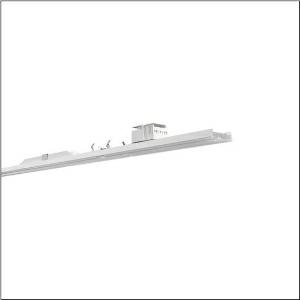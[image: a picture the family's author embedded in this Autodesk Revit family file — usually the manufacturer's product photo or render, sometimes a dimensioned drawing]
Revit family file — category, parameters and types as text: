
# Revit family: licross_r__11_recessed_mo_51tl18cn48xfd_9798
name_source: partatom
category: Lighting Fixtures
units: mm (PartAtom-declared; Revit-internal decimal feet)

## family parameters
Cut with Voids When Loaded = No
Host = Face
Light Source = No
Part Type = Normal
Room Calculation Point = No
Round Connector Dimension = Use Diameter
Shared = No

## types (1)
- --- (1 x LED, 3320 lm, 22.1 W, 4000K)
    Apparent Load = 22 VA
    CIE Flux Codes = 83 96 99 100 100
    Color Rendering = 80
    Color Temperature = 4000K
    Default Elevation = 1800 mm
    Description = Licross® 11 Recessed MOluminaire insert, length: 1.500mm, width: 66mm, height: 67mm, LED rated luminous flux: 8.060lm, light colour: 840, control gear: ON/OFF Multilumen, CLOi, control gear: ECG Multilumen, with plug, 6-pole, with phase selection, mains connection: 220..240V, AC/DC, 0/50..60Hz, without changeover relay, for emergency light function, for central battery installations according to DIN EN 60598-2-22, halogen-free wiring, primary optical cover: cover, of PMMA, light emission: direct distribution, protection rating (complete): IP40, insulation class (complete): insulation class I (protective earthing), certification: CE, ENEC, VDE, protection symbol: D if used in an environment without relevant dust loads with corresponding accessories, permissible ambient temperature for indoor applications: -35..+40°C, standard: EN 60598-2-22, reducing of maximum allowable ambient temperature of 5°C with ceiling mounting, corresponds to IFS (International Featured Standards) requirements for safety and quality in the food industry, packaging unit: 1 piece
    Height = 58 mm
    Lamp = 1 x LED
    Lamp Light Flux = 3320 lm
    Lamp Power = 22.1 W
    Lamp count = 1
    Length = 1500 mm
    Luminous efficacy = 150 lm/W
    Manufacturer = Siteco
    ModVariant = No
    Model = 51TL18CN48XFD
    Mounting Place = Ceiling
    Mounting Type = Pendant
    Number of Poles = 1
    OnlyDefault = Yes
    Power Factor = 1
    Product Name = Licross® 11 Recessed MO
    Product group = luminaire insert
    ProductGroupID = 902
    Protection Class = Protection class I
    Protection Degree = IP 40
    RLX_Detail_Level = 1
    RlxData = <blob elided: 20477 chars, md5=524ba2c6>
    Socket = socket
    Standby Power = 0 W
    System Light Flux = 3320 lm
    System Power = 22 W
    Type Comments = : DC mode (central or group accumulator) initial emergency light level
    Type Image = l_1266722.jpg
    URL = http://relux.com
    VarID = @adj_134167
    Voltage = 0 V
    Weight = 0.00 kg
    Width = 66 mm

## geometry (parser evidence)
native form markers: Blend x4, Sweep x10
no freeform markers — native parametric forms only
